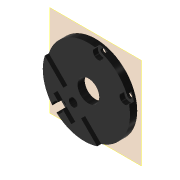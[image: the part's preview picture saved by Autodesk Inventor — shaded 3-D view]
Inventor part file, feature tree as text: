
AUTODESK INVENTOR PART (.ipt)
format: ipt  version: 2022 (Build 260153000, 153)  size: 183,808 bytes
history: native  units: in
note: dims shown in document units (in); Inventor stores cm internally (conversion verified against a paired STEP export)
features: reference x6, other x6, sketch x4, extrude x3, plane x1, hole x1
ambient origin geometry x8: Origin, YZ Plane, XZ Plane, XY Plane, X Axis, Y Axis, Z Axis, Center Point
bodies: Solid1 (feature_tree)
feature tree (21):
  plane  "Work Plane1"
  extrude  "Extrusion1"  TaperAngle=135.0deg  [1 undecoded]
  extrude  "Extrusion2"  Depth=0.0984in TaperAngle=0.0deg
  extrude  "Extrusion3"  Depth=0.1181in TaperAngle=0.0deg
  hole  "Bohrung1"  [1 undecoded]
  sketch  "Sketch1"  dims[d0=0.2756in d1=0.0in d2=135.0deg]
  reference  "Reference1"
  reference  "Reference5"
  reference  "Reference6"
  reference  "Reference7"
  sketch  "Sketch2"  dims[d3=1.5748in d4=0.0984in d5=0.0in]
  sketch  "Sketch3"  dims[d6=0.0039in d7=0.1181in d8=0.0in]
  reference  "Reference8"
  sketch  "Skizze4"  dims[d9=0.126in d10=0.75in d11=0.2559in d12=0.2165in d13=0.5635in d14=1.0in d15=0.8108in]
  reference  "Referenz9"
  other  "<userpath>\Documents\Matchboxscope\INVENTOR\Matchboxscope_v1.iam"
  other  "Matchboxscope_v1.iam"
  other  "Matchboxscope_middle2_v1:1"
  other  "Matchboxscope_Lightperiscope_long_V0:1"
  other  "Matchboxscope_VCM_v1.iam"
  other  "Matchboxscope_middle2_m12VCMLens_v2:1"
note: 2 required parameter values undecoded (feature->parameter linkage not recoverable at this tier; creation-order binding heuristic only, values carry confidence <= 0.55)
